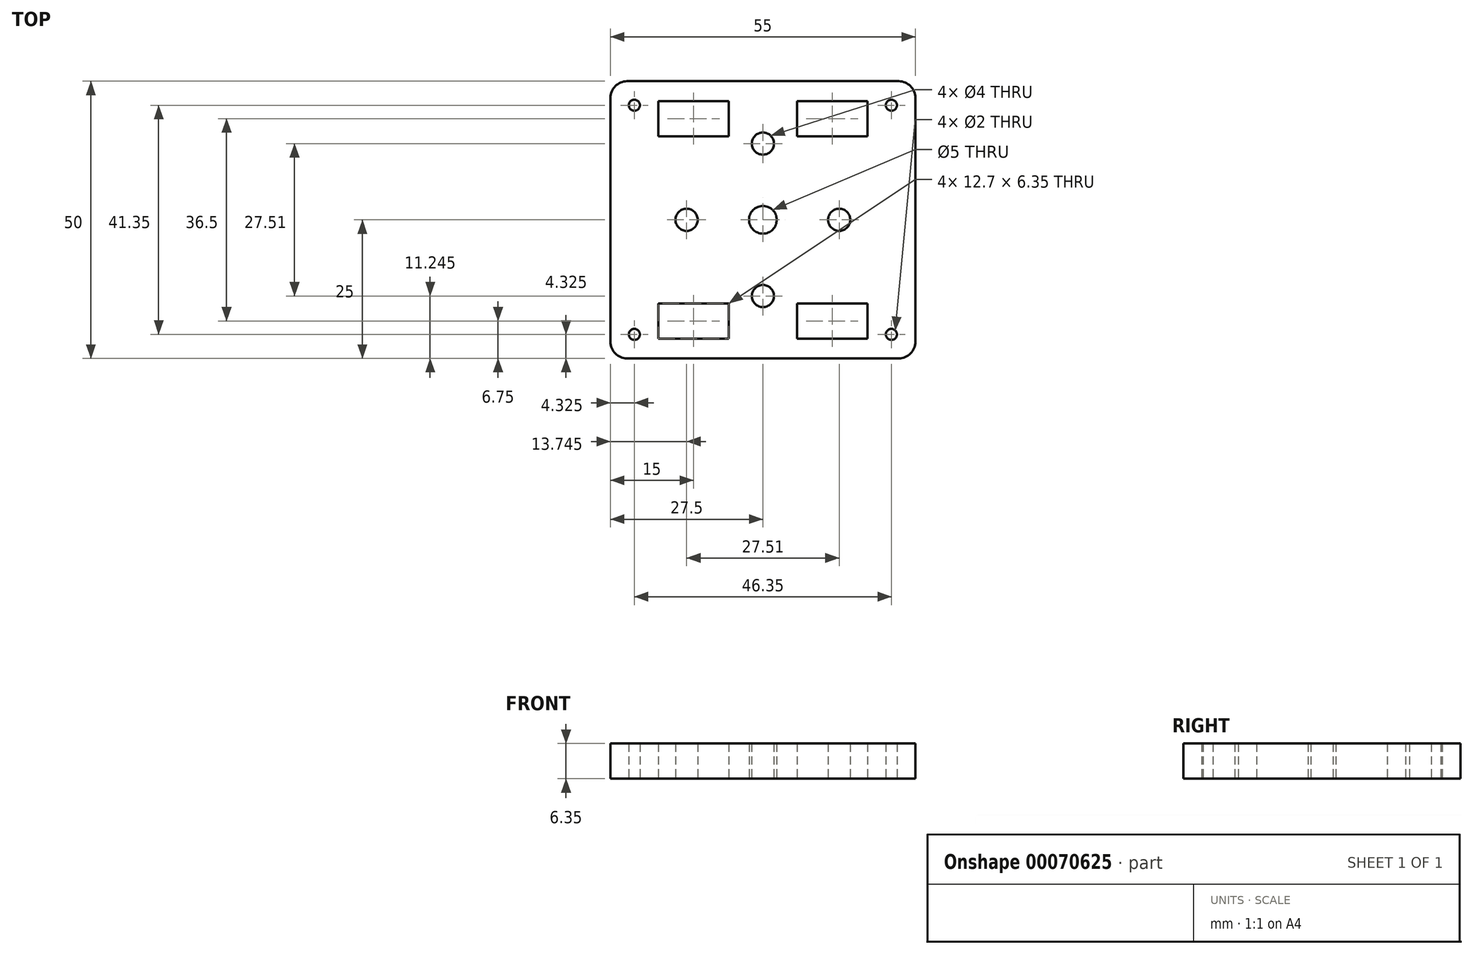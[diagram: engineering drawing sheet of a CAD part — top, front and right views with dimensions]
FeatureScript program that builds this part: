
annotation { "Feature Type Name" : "Feature", "Feature Type Description" : "" }
export const myFeature = defineFeature(function(context is Context, id is Id, definition is map)
    precondition{}
    {
        {
            var Q0;
            Q0=qCreatedBy(makeId("Top.planeOp"),FACE);
            var sketch = newSketch(context, id + "F0", { "sketchPlane" : qUnion([Q0])});
            skLineSegment(sketch, "E0", {"start": v(0, 0) * mm, "end": v(0, 27.13) * mm});
            skLineSegment(sketch, "E1.bottom", {"start": v(-27.5, 25) * mm, "end": v(27.5, 25) * mm});
            skLineSegment(sketch, "E1.top", {"start": v(-27.5, -25) * mm, "end": v(27.5, -25) * mm});
            skLineSegment(sketch, "E1.left", {"start": v(-27.5, 25) * mm, "end": v(-27.5, -25) * mm});
            skLineSegment(sketch, "E1.right", {"start": v(27.5, 25) * mm, "end": v(27.5, -25) * mm});
            skLineSegment(sketch, "E2.bottom", {"start": v(-18.85, 21.43) * mm, "end": v(-6.15, 21.43) * mm});
            skLineSegment(sketch, "E2.top", {"start": v(-18.85, 15.07) * mm, "end": v(-6.15, 15.07) * mm});
            skLineSegment(sketch, "E2.left", {"start": v(-18.85, 21.43) * mm, "end": v(-18.85, 15.07) * mm});
            skLineSegment(sketch, "E2.right", {"start": v(-6.15, 21.43) * mm, "end": v(-6.15, 15.07) * mm});
            skPoint(sketch, "E3", {"position": v(-12.5, 21.43) * mm});
            skLineSegment(sketch, "E4.0.1.0", {"start": v(-18.85, -21.43) * mm, "end": v(-6.15, -21.43) * mm});
            skLineSegment(sketch, "E4.0.1.1", {"start": v(-18.85, -15.07) * mm, "end": v(-6.15, -15.07) * mm});
            skLineSegment(sketch, "E4.0.1.2", {"start": v(-18.85, -15.07) * mm, "end": v(-18.85, -21.43) * mm});
            skLineSegment(sketch, "E4.0.1.3", {"start": v(-6.15, -15.07) * mm, "end": v(-6.15, -21.43) * mm});
            skPoint(sketch, "E4.0.1.4", {"position": v(-12.5, -15.07) * mm});
            skLineSegment(sketch, "E4.1.0.0", {"start": v(6.15, 15.07) * mm, "end": v(18.85, 15.07) * mm});
            skLineSegment(sketch, "E4.1.0.1", {"start": v(6.15, 21.43) * mm, "end": v(18.85, 21.43) * mm});
            skLineSegment(sketch, "E4.1.0.2", {"start": v(6.15, 21.43) * mm, "end": v(6.15, 15.07) * mm});
            skLineSegment(sketch, "E4.1.0.3", {"start": v(18.85, 21.43) * mm, "end": v(18.85, 15.07) * mm});
            skPoint(sketch, "E4.1.0.4", {"position": v(12.5, 21.43) * mm});
            skLineSegment(sketch, "E4.1.1.0", {"start": v(6.15, -21.43) * mm, "end": v(18.85, -21.43) * mm});
            skLineSegment(sketch, "E4.1.1.1", {"start": v(6.15, -15.07) * mm, "end": v(18.85, -15.07) * mm});
            skLineSegment(sketch, "E4.1.1.2", {"start": v(6.15, -15.07) * mm, "end": v(6.15, -21.43) * mm});
            skLineSegment(sketch, "E4.1.1.3", {"start": v(18.85, -15.07) * mm, "end": v(18.85, -21.43) * mm});
            skPoint(sketch, "E4.1.1.4", {"position": v(12.5, -15.07) * mm});
            skLineSegment(sketch, "E4.direction1", {"start": v(-18.85, 15.07) * mm, "end": v(6.15, 15.07) * mm, "construction": true});
            skLineSegment(sketch, "E4.direction2", {"start": v(-18.85, 15.07) * mm, "end": v(-18.85, -21.43) * mm, "construction": true});
            skPoint(sketch, "E5", {"position": v(0, -13.76) * mm});
            skPoint(sketch, "E6.1.0", {"position": v(13.75, 0) * mm});
            skPoint(sketch, "E6.center", {"position": v(0, 0) * mm});
            skPoint(sketch, "E7.0.2.0", {"position": v(0, 13.76) * mm});
            skPoint(sketch, "E8.0.3.0", {"position": v(-13.76, 0) * mm});
            skPoint(sketch, "E9", {"position": v(-23.18, 20.68) * mm});
            skPoint(sketch, "E10.MirrorP", {"position": v(23.18, 20.68) * mm});
            skPoint(sketch, "E11.MirrorP", {"position": v(23.18, -20.68) * mm});
            skPoint(sketch, "E12.MirrorP", {"position": v(-23.18, -20.68) * mm});
            skSolve(sketch);
        }
        {
            var Q0;
            Q0=makeQuery(id+"F0.imprint","IMPRINT",FACE,{"disambiguationData":[TD([[makeQuery(id+"F0.imprint","IMPRINT",EDGE,{"derivedFrom":sQuery(id+"F0.wireOp",EDGE,"E1.top")}),1.0]])]});
            extrude(context, id + "F1", {"entities" : qUnion([Q0]), "depth" : 6.35 * mm});
        }
        {
            var Q0;
            Q0=makeQuery(id+"F1.opExtrude","SWEPT_EDGE",EDGE,{"disambiguationData":[OSD([sQuery(id+"F0.wireOp",EDGE,"E1.top"),sQuery(id+"F0.wireOp",EDGE,"E1.right")])]});
            var Q1;
            Q1=makeQuery(id+"F1.opExtrude","SWEPT_EDGE",EDGE,{"disambiguationData":[OSD([sQuery(id+"F0.wireOp",EDGE,"E1.bottom"),sQuery(id+"F0.wireOp",EDGE,"E1.right")])]});
            var Q2;
            Q2=makeQuery(id+"F1.opExtrude","SWEPT_EDGE",EDGE,{"disambiguationData":[OSD([sQuery(id+"F0.wireOp",EDGE,"E1.top"),sQuery(id+"F0.wireOp",EDGE,"E1.left")])]});
            var Q3;
            Q3=makeQuery(id+"F1.opExtrude","SWEPT_EDGE",EDGE,{"disambiguationData":[OSD([sQuery(id+"F0.wireOp",EDGE,"E1.bottom"),sQuery(id+"F0.wireOp",EDGE,"E1.left")])]});
            fillet(context, id + "F2", {"entities" : qUnion([Q0, Q1, Q2, Q3]), "radius" : 3 * mm, "tangentPropagation" : true, "allowEdgeOverflow" : false});
        }
        {
            var Q0;
            Q0=sQuery(id+"F0.wireOp",VERTEX,"E0.start");
            var Q1;
            Q1=makeQuery(id+"F1.opExtrude","SWEPT_BODY",BODY,{"disambiguationData":[OSD([sQuery(id+"F0.wireOp",EDGE,"E1.bottom"),sQuery(id+"F0.wireOp",EDGE,"E1.top"),sQuery(id+"F0.wireOp",EDGE,"E1.left"),sQuery(id+"F0.wireOp",EDGE,"E1.right"),sQuery(id+"F0.wireOp",EDGE,"E2.bottom"),sQuery(id+"F0.wireOp",EDGE,"E2.top"),sQuery(id+"F0.wireOp",EDGE,"E2.left"),sQuery(id+"F0.wireOp",EDGE,"E2.right"),sQuery(id+"F0.wireOp",EDGE,"E4.0.1.0"),sQuery(id+"F0.wireOp",EDGE,"E4.0.1.1"),sQuery(id+"F0.wireOp",EDGE,"E4.0.1.2"),sQuery(id+"F0.wireOp",EDGE,"E4.0.1.3"),sQuery(id+"F0.wireOp",EDGE,"E4.1.0.0"),sQuery(id+"F0.wireOp",EDGE,"E4.1.0.1"),sQuery(id+"F0.wireOp",EDGE,"E4.1.0.2"),sQuery(id+"F0.wireOp",EDGE,"E4.1.0.3"),sQuery(id+"F0.wireOp",EDGE,"E4.1.1.0"),sQuery(id+"F0.wireOp",EDGE,"E4.1.1.1"),sQuery(id+"F0.wireOp",EDGE,"E4.1.1.2"),sQuery(id+"F0.wireOp",EDGE,"E4.1.1.3")])]});
            hole(context, id + "F3", {"style" : HoleStyle.SIMPLE, "endStyle" : HoleEndStyle.THROUGH, "oppositeDirection" : true, "holeDiameter" : 5 * mm, "locations" : qUnion([Q0]), "scope" : qUnion([Q1]), "isTappedThrough" : true});
        }
        {
            var Q0;
            Q0=sQuery(id+"F0.wireOp",VERTEX,"E8.0.3.0");
            var Q1;
            Q1=sQuery(id+"F0.wireOp",VERTEX,"E5");
            var Q2;
            Q2=sQuery(id+"F0.wireOp",VERTEX,"E6.1.0");
            var Q3;
            Q3=sQuery(id+"F0.wireOp",VERTEX,"E7.0.2.0");
            var Q4;
            Q4=makeQuery(id+"F1.opExtrude","SWEPT_BODY",BODY,{"disambiguationData":[OSD([sQuery(id+"F0.wireOp",EDGE,"E1.bottom"),sQuery(id+"F0.wireOp",EDGE,"E1.top"),sQuery(id+"F0.wireOp",EDGE,"E1.left"),sQuery(id+"F0.wireOp",EDGE,"E1.right"),sQuery(id+"F0.wireOp",EDGE,"E2.bottom"),sQuery(id+"F0.wireOp",EDGE,"E2.top"),sQuery(id+"F0.wireOp",EDGE,"E2.left"),sQuery(id+"F0.wireOp",EDGE,"E2.right"),sQuery(id+"F0.wireOp",EDGE,"E4.0.1.0"),sQuery(id+"F0.wireOp",EDGE,"E4.0.1.1"),sQuery(id+"F0.wireOp",EDGE,"E4.0.1.2"),sQuery(id+"F0.wireOp",EDGE,"E4.0.1.3"),sQuery(id+"F0.wireOp",EDGE,"E4.1.0.0"),sQuery(id+"F0.wireOp",EDGE,"E4.1.0.1"),sQuery(id+"F0.wireOp",EDGE,"E4.1.0.2"),sQuery(id+"F0.wireOp",EDGE,"E4.1.0.3"),sQuery(id+"F0.wireOp",EDGE,"E4.1.1.0"),sQuery(id+"F0.wireOp",EDGE,"E4.1.1.1"),sQuery(id+"F0.wireOp",EDGE,"E4.1.1.2"),sQuery(id+"F0.wireOp",EDGE,"E4.1.1.3")])]});
            hole(context, id + "F4", {"style" : HoleStyle.SIMPLE, "endStyle" : HoleEndStyle.THROUGH, "oppositeDirection" : true, "holeDiameter" : 4 * mm, "locations" : qUnion([Q0, Q1, Q2, Q3]), "scope" : qUnion([Q4]), "isTappedThrough" : true});
        }
        {
            var Q0;
            Q0=sQuery(id+"F0.wireOp",VERTEX,"E9");
            var Q1;
            Q1=sQuery(id+"F0.wireOp",VERTEX,"E10.MirrorP");
            var Q2;
            Q2=sQuery(id+"F0.wireOp",VERTEX,"E11.MirrorP");
            var Q3;
            Q3=sQuery(id+"F0.wireOp",VERTEX,"E12.MirrorP");
            var Q4;
            Q4=makeQuery(id+"F1.opExtrude","SWEPT_BODY",BODY,{"disambiguationData":[OSD([sQuery(id+"F0.wireOp",EDGE,"E1.bottom"),sQuery(id+"F0.wireOp",EDGE,"E1.top"),sQuery(id+"F0.wireOp",EDGE,"E1.left"),sQuery(id+"F0.wireOp",EDGE,"E1.right"),sQuery(id+"F0.wireOp",EDGE,"E2.bottom"),sQuery(id+"F0.wireOp",EDGE,"E2.top"),sQuery(id+"F0.wireOp",EDGE,"E2.left"),sQuery(id+"F0.wireOp",EDGE,"E2.right"),sQuery(id+"F0.wireOp",EDGE,"E4.0.1.0"),sQuery(id+"F0.wireOp",EDGE,"E4.0.1.1"),sQuery(id+"F0.wireOp",EDGE,"E4.0.1.2"),sQuery(id+"F0.wireOp",EDGE,"E4.0.1.3"),sQuery(id+"F0.wireOp",EDGE,"E4.1.0.0"),sQuery(id+"F0.wireOp",EDGE,"E4.1.0.1"),sQuery(id+"F0.wireOp",EDGE,"E4.1.0.2"),sQuery(id+"F0.wireOp",EDGE,"E4.1.0.3"),sQuery(id+"F0.wireOp",EDGE,"E4.1.1.0"),sQuery(id+"F0.wireOp",EDGE,"E4.1.1.1"),sQuery(id+"F0.wireOp",EDGE,"E4.1.1.2"),sQuery(id+"F0.wireOp",EDGE,"E4.1.1.3")])]});
            hole(context, id + "F5", {"style" : HoleStyle.SIMPLE, "endStyle" : HoleEndStyle.THROUGH, "oppositeDirection" : true, "holeDiameter" : 2 * mm, "locations" : qUnion([Q0, Q1, Q2, Q3]), "scope" : qUnion([Q4]), "isTappedThrough" : true});
        }
    });
